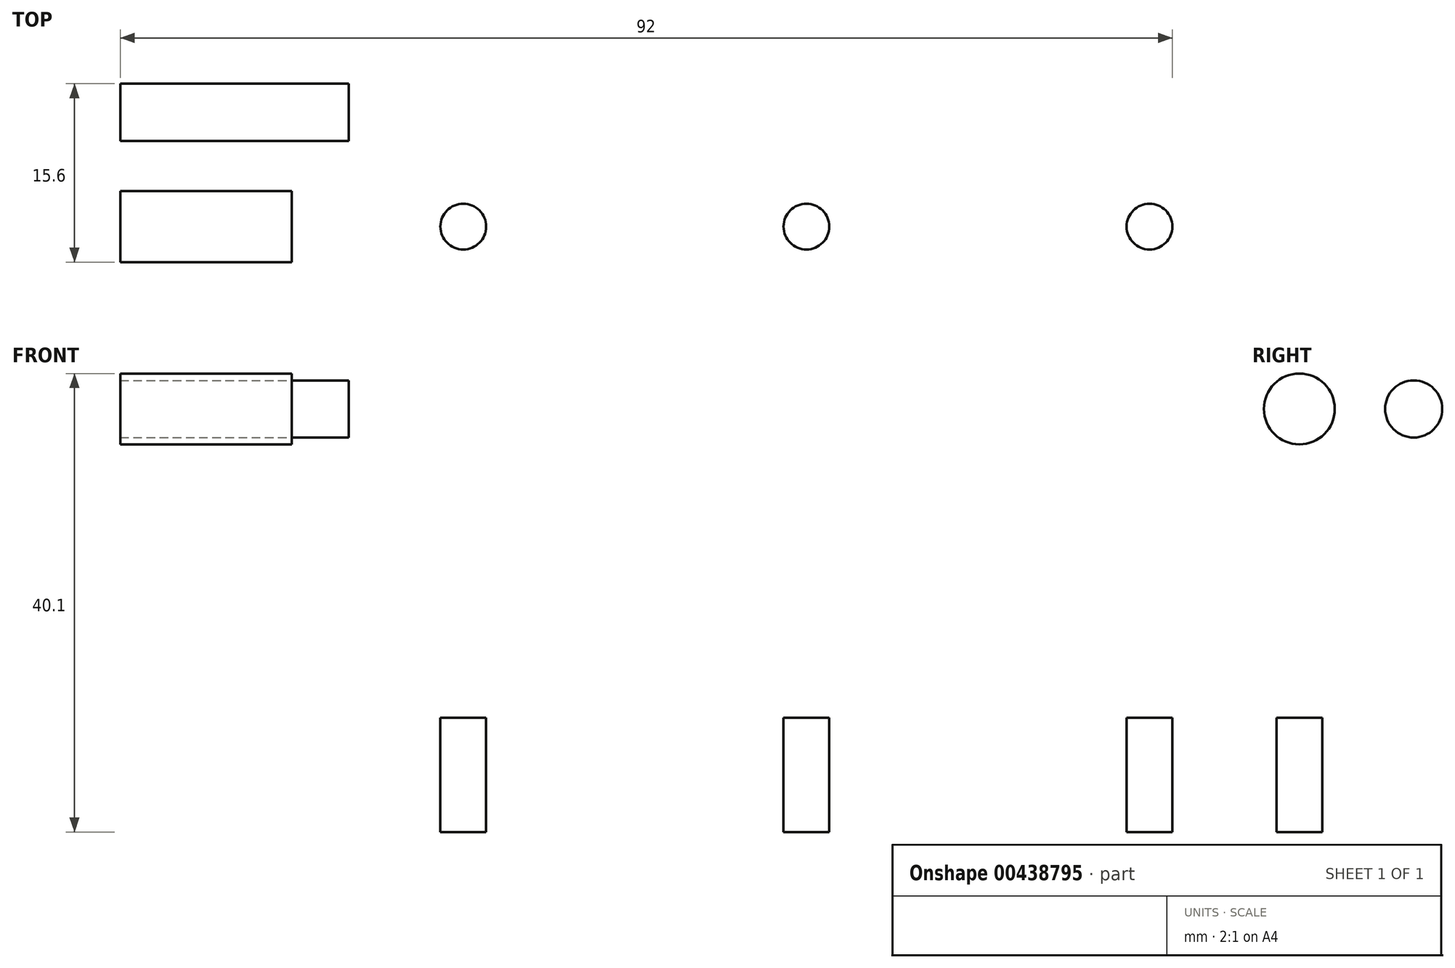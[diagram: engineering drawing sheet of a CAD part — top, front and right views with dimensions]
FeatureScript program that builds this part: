
annotation { "Feature Type Name" : "Feature", "Feature Type Description" : "" }
export const myFeature = defineFeature(function(context is Context, id is Id, definition is map)
    precondition{}
    {
        {
            var Q0;
            Q0=qCreatedBy(makeId("Front.planeOp"),FACE);
            var sketch = newSketch(context, id + "F0", { "sketchPlane" : qUnion([Q0])});
            skLineSegment(sketch, "E0.bottom", {"start": v(110, -25) * mm, "end": v(-110, -25) * mm});
            skLineSegment(sketch, "E0.left", {"start": v(110, -25) * mm, "end": v(110, -15) * mm});
            skLineSegment(sketch, "E0.right", {"start": v(-110, -25) * mm, "end": v(-110, 25) * mm});
            skPoint(sketch, "E0.middle", {"position": v(0, 0) * mm});
            skLineSegment(sketch, "E1", {"start": v(-90, 25) * mm, "end": v(-90, -15) * mm});
            skLineSegment(sketch, "E2", {"start": v(-90, -15) * mm, "end": v(110, -15) * mm});
            skLineSegment(sketch, "E3.trimOffspring", {"start": v(-90, 25) * mm, "end": v(-110, 25) * mm});
            skSolve(sketch);
        }
        {
            var Q0;
            Q0 = qSketchRegion(id + "F0", true);
            extrude(context, id + "F1", {"entities" : qUnion([Q0]), "depth" : 80 * mm});
        }
        {
            var Q0;
            Q0=makeQuery(id+"F1.opExtrude","SWEPT_FACE",FACE,{"disambiguationData":[OSD([sQuery(id+"F0.wireOp",EDGE,"E2")])]});
            var sketch = newSketch(context, id + "F2", { "sketchPlane" : qUnion([Q0])});
            skPoint(sketch, "E4.centerSnap0", {"position": v(110, -40) * mm});
            skLineSegment(sketch, "E5", {"start": v(10, -80) * mm, "end": v(10, 11.62) * mm, "construction": true});
            skCircle(sketch, "E6", {"center": v(10, -40) * mm, "radius": 2 * mm});
            skCircle(sketch, "E7", {"center": v(40, -40) * mm, "radius": 2 * mm});
            skCircle(sketch, "E8", {"center": v(70, -40) * mm, "radius": 2 * mm});
            skCircle(sketch, "E9", {"center": v(100, -40) * mm, "radius": 2 * mm});
            skCircle(sketch, "E10.MirrorC", {"center": v(-20, -40) * mm, "radius": 2 * mm});
            skCircle(sketch, "E11.MirrorC", {"center": v(-50, -40) * mm, "radius": 2 * mm});
            skCircle(sketch, "E12.MirrorC", {"center": v(-80, -40) * mm, "radius": 2 * mm});
            skLineSegment(sketch, "E13", {"start": v(-90, -40) * mm, "end": v(116.49, -40) * mm, "construction": true});
            skSolve(sketch);
        }
        {
            var Q0;
            Q0=makeQuery(id+"F2.imprint","IMPRINT",FACE,{"disambiguationData":[TD([[makeQuery(id+"F2.imprint","IMPRINT",EDGE,{"derivedFrom":sQuery(id+"F2.wireOp",EDGE,"E12.MirrorC")}),-1.0]])]});
            var Q1;
            Q1=makeQuery(id+"F2.imprint","IMPRINT",FACE,{"disambiguationData":[TD([[makeQuery(id+"F2.imprint","IMPRINT",EDGE,{"derivedFrom":sQuery(id+"F2.wireOp",EDGE,"E11.MirrorC")}),-1.0]])]});
            var Q2;
            Q2=makeQuery(id+"F2.imprint","IMPRINT",FACE,{"disambiguationData":[TD([[makeQuery(id+"F2.imprint","IMPRINT",EDGE,{"derivedFrom":sQuery(id+"F2.wireOp",EDGE,"E10.MirrorC")}),-1.0]])]});
            var Q3;
            Q3=makeQuery(id+"F2.imprint","IMPRINT",FACE,{"disambiguationData":[TD([[makeQuery(id+"F2.imprint","IMPRINT",EDGE,{"derivedFrom":sQuery(id+"F2.wireOp",EDGE,"E6")}),1.0]])]});
            var Q4;
            Q4=makeQuery(id+"F2.imprint","IMPRINT",FACE,{"disambiguationData":[TD([[makeQuery(id+"F2.imprint","IMPRINT",EDGE,{"derivedFrom":sQuery(id+"F2.wireOp",EDGE,"E7")}),1.0]])]});
            var Q5;
            Q5=makeQuery(id+"F2.imprint","IMPRINT",FACE,{"disambiguationData":[TD([[makeQuery(id+"F2.imprint","IMPRINT",EDGE,{"derivedFrom":sQuery(id+"F2.wireOp",EDGE,"E8")}),1.0]])]});
            var Q6;
            Q6=makeQuery(id+"F2.imprint","IMPRINT",FACE,{"disambiguationData":[TD([[makeQuery(id+"F2.imprint","IMPRINT",EDGE,{"derivedFrom":sQuery(id+"F2.wireOp",EDGE,"E9")}),1.0]])]});
            var Q7;
            Q7=makeQuery(id+"F2.imprint","IMPRINT",FACE,{"disambiguationData":[TD([[makeQuery(id+"F2.imprint","IMPRINT",EDGE,{"derivedFrom":sQuery(id+"F2.wireOp",EDGE,"c41c5453-e8bb-4a3e-9557-25ee7b66b4700.MirrorC")}),-1.0]])]});
            var Q8;
            Q8=makeQuery(id+"F2.imprint","IMPRINT",FACE,{"disambiguationData":[TD([[makeQuery(id+"F2.imprint","IMPRINT",EDGE,{"derivedFrom":sQuery(id+"F2.wireOp",EDGE,"I7Iwlpyc-8dGm-e3G4-TlpB-zGxiDb6e0fvW")}),1.0]])]});
            var Q9;
            Q9=makeQuery(id+"F2.imprint","IMPRINT",FACE,{"disambiguationData":[TD([[makeQuery(id+"F2.imprint","IMPRINT",EDGE,{"derivedFrom":sQuery(id+"F2.wireOp",EDGE,"f8492685-fc9f-4306-81cc-d36f9e60aca60.MirrorC")}),-1.0]])]});
            var Q10;
            Q10=makeQuery(id+"F2.imprint","IMPRINT",FACE,{"disambiguationData":[TD([[makeQuery(id+"F2.imprint","IMPRINT",EDGE,{"derivedFrom":sQuery(id+"F2.wireOp",EDGE,"a1a9ff02-7ac0-4a9d-86e0-a633f2fdac420.MirrorC")}),-1.0]])]});
            var Q11;
            Q11=makeQuery(id+"F2.imprint","IMPRINT",FACE,{"disambiguationData":[TD([[makeQuery(id+"F2.imprint","IMPRINT",EDGE,{"derivedFrom":sQuery(id+"F2.wireOp",EDGE,"2728e923-fd88-408f-9164-2003a942d9010.MirrorC")}),-1.0]])]});
            var Q12;
            Q12=makeQuery(id+"F2.imprint","IMPRINT",FACE,{"disambiguationData":[TD([[makeQuery(id+"F2.imprint","IMPRINT",EDGE,{"derivedFrom":sQuery(id+"F2.wireOp",EDGE,"c6c43076-e072-4698-a444-2f6bf67824110.MirrorC")}),-1.0]])]});
            var Q13;
            Q13=makeQuery(id+"F2.imprint","IMPRINT",FACE,{"disambiguationData":[TD([[makeQuery(id+"F2.imprint","IMPRINT",EDGE,{"derivedFrom":sQuery(id+"F2.wireOp",EDGE,"b80fdb68-9bb9-45bf-a2d1-23460f088d310.MirrorC")}),1.0]])]});
            var Q14;
            Q14=makeQuery(id+"F2.imprint","IMPRINT",FACE,{"disambiguationData":[TD([[makeQuery(id+"F2.imprint","IMPRINT",EDGE,{"derivedFrom":sQuery(id+"F2.wireOp",EDGE,"a2eeff7d-b5c2-4593-8df5-8ecde90cd1300.MirrorC")}),1.0]])]});
            var Q15;
            Q15=makeQuery(id+"F2.imprint","IMPRINT",FACE,{"disambiguationData":[TD([[makeQuery(id+"F2.imprint","IMPRINT",EDGE,{"derivedFrom":sQuery(id+"F2.wireOp",EDGE,"5641b989-e42e-47eb-99f7-84fa131d900c0.MirrorC")}),1.0]])]});
            var Q16;
            Q16=makeQuery(id+"F2.imprint","IMPRINT",FACE,{"disambiguationData":[TD([[makeQuery(id+"F2.imprint","IMPRINT",EDGE,{"derivedFrom":sQuery(id+"F2.wireOp",EDGE,"ca76e5ea-a235-47b5-b9a3-303670e906dd0.MirrorC")}),1.0]])]});
            var Q17;
            Q17=makeQuery(id+"F2.imprint","IMPRINT",FACE,{"disambiguationData":[TD([[makeQuery(id+"F2.imprint","IMPRINT",EDGE,{"derivedFrom":sQuery(id+"F2.wireOp",EDGE,"19209c2f-43ef-4d16-a487-0c1452ed7faf0.MirrorC")}),-1.0]])]});
            var Q18;
            Q18=makeQuery(id+"F2.imprint","IMPRINT",FACE,{"disambiguationData":[TD([[makeQuery(id+"F2.imprint","IMPRINT",EDGE,{"derivedFrom":sQuery(id+"F2.wireOp",EDGE,"7fbd108f-97a8-406c-bced-151d589b28e90.MirrorC")}),-1.0]])]});
            var Q19;
            Q19=makeQuery(id+"F2.imprint","IMPRINT",FACE,{"disambiguationData":[TD([[makeQuery(id+"F2.imprint","IMPRINT",EDGE,{"derivedFrom":sQuery(id+"F2.wireOp",EDGE,"6494d87a-d47d-4a4f-8da2-39e12109fe580.MirrorC")}),-1.0]])]});
            var Q20;
            Q20=makeQuery(id+"F2.imprint","IMPRINT",FACE,{"disambiguationData":[TD([[makeQuery(id+"F2.imprint","IMPRINT",EDGE,{"derivedFrom":sQuery(id+"F2.wireOp",EDGE,"e7247889-a87d-4bfb-beb1-c40833b5bef20.MirrorC")}),-1.0]])]});
            var Q21;
            Q21=makeQuery(id+"F2.imprint","IMPRINT",FACE,{"disambiguationData":[TD([[makeQuery(id+"F2.imprint","IMPRINT",EDGE,{"derivedFrom":sQuery(id+"F2.wireOp",EDGE,"93KI5OKB-R7Rc-e17z-F2rg-B4bQ0ffBtoF9")}),1.0]])]});
            var Q22;
            Q22=makeQuery(id+"F2.imprint","IMPRINT",FACE,{"disambiguationData":[TD([[makeQuery(id+"F2.imprint","IMPRINT",EDGE,{"derivedFrom":sQuery(id+"F2.wireOp",EDGE,"nX192IQH-xTf9-Jyna-HGiK-nnlijm6KJFIf")}),1.0]])]});
            var Q23;
            Q23=makeQuery(id+"F2.imprint","IMPRINT",FACE,{"disambiguationData":[TD([[makeQuery(id+"F2.imprint","IMPRINT",EDGE,{"derivedFrom":sQuery(id+"F2.wireOp",EDGE,"CWDS7qFT-89qx-fdw9-0woP-oGRWJPSfgCDu")}),1.0]])]});
            var Q24;
            Q24=makeQuery(id+"F2.imprint","IMPRINT",FACE,{"disambiguationData":[TD([[makeQuery(id+"F2.imprint","IMPRINT",EDGE,{"derivedFrom":sQuery(id+"F2.wireOp",EDGE,"UBkpufn3-6le9-jO30-NMnS-uYkfcgU9BDeI")}),1.0]])]});
            extrude(context, id + "F3", {"entities" : qUnion([Q0, Q1, Q2, Q3, Q4, Q5, Q6, Q7, Q8, Q9, Q10, Q11, Q12, Q13, Q14, Q15, Q16, Q17, Q18, Q19, Q20, Q21, Q22, Q23, Q24]), "operationType" : NewBodyOperationType.REMOVE, "oppositeDirection" : true, "depth" : 25 * mm});
        }
        {
            var Q0;
            Q0=makeQuery(id+"F1.opExtrude","SWEPT_FACE",FACE,{"disambiguationData":[OSD([sQuery(id+"F0.wireOp",EDGE,"E1")])]});
            var sketch = newSketch(context, id + "F4", { "sketchPlane" : qUnion([Q0])});
            skCircle(sketch, "E14", {"center": v(-50, 12) * mm, "radius": 2.5 * mm});
            skLineSegment(sketch, "E15", {"start": v(-40, 25) * mm, "end": v(-40, -10.35) * mm, "construction": true});
            skCircle(sketch, "E16.MirrorC", {"center": v(-30, 12) * mm, "radius": 2.5 * mm});
            skCircle(sketch, "E17", {"center": v(-40, 12) * mm, "radius": 3.1 * mm});
            skSolve(sketch);
        }
        {
            var Q0;
            Q0=makeQuery(id+"F4.imprint","IMPRINT",FACE,{"disambiguationData":[TD([[makeQuery(id+"F4.imprint","IMPRINT",EDGE,{"derivedFrom":sQuery(id+"F4.wireOp",EDGE,"E14")}),1.0]])]});
            var Q1;
            Q1=makeQuery(id+"F4.imprint","IMPRINT",FACE,{"disambiguationData":[TD([[makeQuery(id+"F4.imprint","IMPRINT",EDGE,{"derivedFrom":sQuery(id+"F4.wireOp",EDGE,"E16.MirrorC")}),-1.0]])]});
            extrude(context, id + "F5", {"entities" : qUnion([Q0, Q1]), "operationType" : NewBodyOperationType.REMOVE, "oppositeDirection" : true, "depth" : 22 * mm, "offsetDistance" : 25 * mm});
        }
        {
            var Q0;
            Q0=makeQuery(id+"F4.imprint","IMPRINT",FACE,{"disambiguationData":[TD([[makeQuery(id+"F4.imprint","IMPRINT",EDGE,{"derivedFrom":sQuery(id+"F4.wireOp",EDGE,"E17")}),1.0]])]});
            extrude(context, id + "F6", {"entities" : qUnion([Q0]), "operationType" : NewBodyOperationType.REMOVE, "oppositeDirection" : true, "depth" : 5 * mm, "offsetDistance" : 25 * mm});
        }
    });
